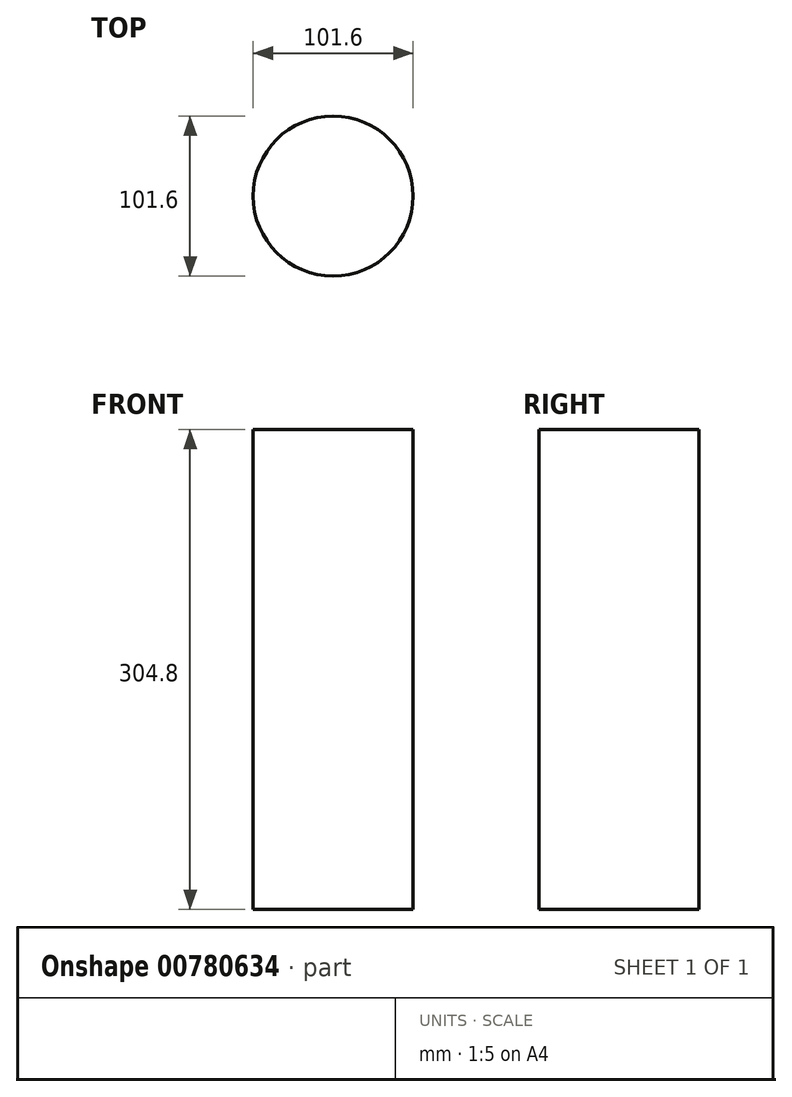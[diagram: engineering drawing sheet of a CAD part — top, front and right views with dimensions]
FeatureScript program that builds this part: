
annotation { "Feature Type Name" : "Feature", "Feature Type Description" : "" }
export const myFeature = defineFeature(function(context is Context, id is Id, definition is map)
    precondition{}
    {
        {
            var Q0;
            Q0=qCreatedBy(makeId("Top.planeOp"),FACE);
            var sketch = newSketch(context, id + "F0", { "sketchPlane" : qUnion([Q0])});
            skCircle(sketch, "E0", {"center": v(0, 0) * mm, "radius": 50.8 * mm});
            skSolve(sketch);
        }
        {
            var Q0;
            Q0=makeQuery(id+"F0.imprint","IMPRINT",FACE,{"disambiguationData":[TD([[makeQuery(id+"F0.imprint","IMPRINT",EDGE,{"derivedFrom":sQuery(id+"F0.wireOp",EDGE,"E0")}),1.0]])]});
            extrude(context, id + "F1", {"entities" : qUnion([Q0]), "depth" : 304.8 * mm, "offsetDistance" : 25.4 * mm});
        }
    });
